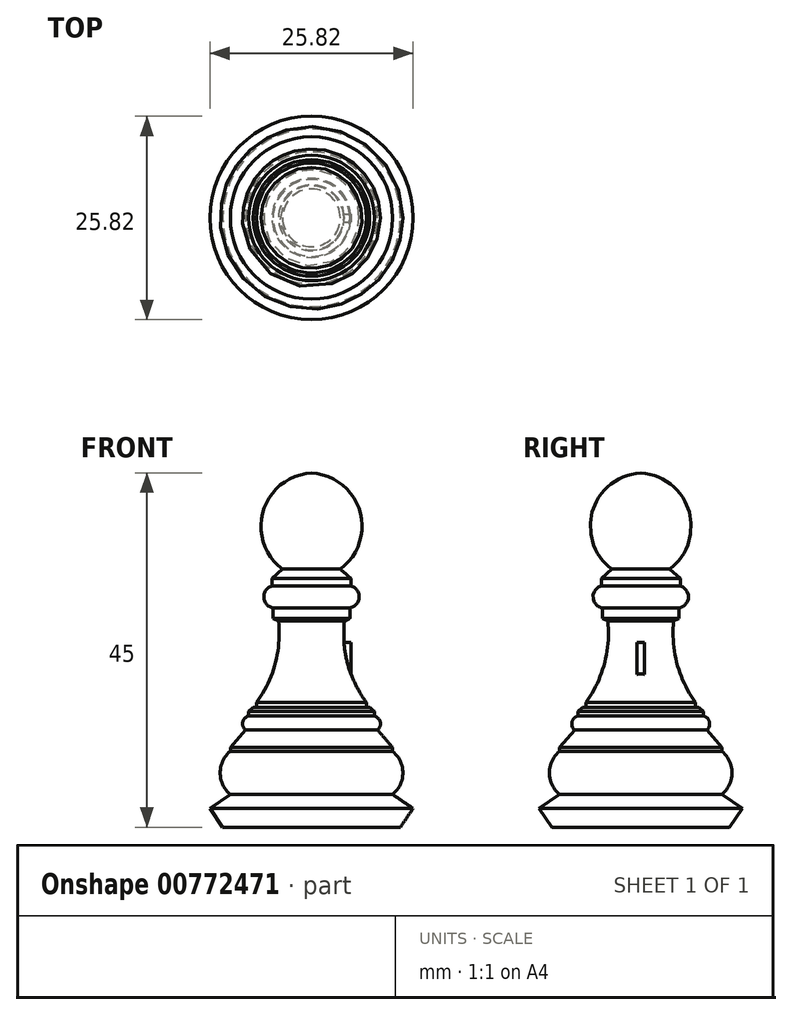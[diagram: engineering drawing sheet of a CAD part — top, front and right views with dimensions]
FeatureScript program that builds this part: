
annotation { "Feature Type Name" : "Feature", "Feature Type Description" : "" }
export const myFeature = defineFeature(function(context is Context, id is Id, definition is map)
    precondition{}
    {
        {
            var Q0;
            Q0=qCreatedBy(makeId("Front.planeOp"),FACE);
            var sketch = newSketch(context, id + "F0", { "sketchPlane" : qUnion([Q0])});
            skLineSegment(sketch, "E0", {"start": v(0, 0) * mm, "end": v(11.29, 0) * mm});
            skLineSegment(sketch, "E1", {"start": v(11.29, 0) * mm, "end": v(12.91, 2.4) * mm});
            skLineSegment(sketch, "E2", {"start": v(12.91, 2.4) * mm, "end": v(10.31, 4.16) * mm});
            skArc(sketch, "E3", {"start": v(10.31, 4.16) * mm, "mid": v(11.6, 6.9) * mm, "end": v(10.31, 9.66) * mm});
            skLineSegment(sketch, "E4", {"start": v(10.31, 9.66) * mm, "end": v(10.31, 10.13) * mm});
            skLineSegment(sketch, "E5", {"start": v(10.31, 10.13) * mm, "end": v(8.38, 12.37) * mm});
            skArc(sketch, "E6", {"start": v(8.38, 12.37) * mm, "mid": v(8.73, 13.38) * mm, "end": v(7.97, 14.14) * mm});
            skLineSegment(sketch, "E7", {"start": v(7.97, 14.14) * mm, "end": v(7.97, 14.74) * mm});
            skLineSegment(sketch, "E8", {"start": v(7.97, 14.74) * mm, "end": v(7.4, 15.25) * mm});
            skLineSegment(sketch, "E9", {"start": v(7.4, 15.25) * mm, "end": v(6.98, 15.25) * mm});
            skLineSegment(sketch, "E10", {"start": v(6.98, 15.83) * mm, "end": v(6.98, 15.25) * mm});
            skArc(sketch, "E11", {"start": v(4.18, 26.19) * mm, "mid": v(4.62, 20.75) * mm, "end": v(6.98, 15.83) * mm});
            skLineSegment(sketch, "E12", {"start": v(4.18, 26.19) * mm, "end": v(4.89, 26.5) * mm});
            skLineSegment(sketch, "E13", {"start": v(4.89, 26.5) * mm, "end": v(4.89, 27.86) * mm});
            skLineSegment(sketch, "E14", {"start": v(5.01, 30.66) * mm, "end": v(5.01, 31.6) * mm});
            skLineSegment(sketch, "E15", {"start": v(5.01, 31.6) * mm, "end": v(3.67, 32.8) * mm});
            skArc(sketch, "E16", {"start": v(3.67, 32.8) * mm, "mid": v(6.13, 40.19) * mm, "end": v(0, 45) * mm});
            skLineSegment(sketch, "E17", {"start": v(0, 45) * mm, "end": v(0, 0) * mm});
            skArc(sketch, "E18", {"start": v(4.89, 27.86) * mm, "mid": v(6.05, 29.2) * mm, "end": v(5.01, 30.66) * mm});
            skSolve(sketch);
        }
        {
            var Q0;
            Q0 = qSketchRegion(id + "F0", true);
            var Q1;
            Q1=sQuery(id+"F0.wireOp",EDGE,"E17");
            revolve(context, id + "F1", {"surfaceOperationType" : NewSurfaceOperationType.NEW, "entities" : qUnion([Q0]), "axis" : qUnion([Q1]), "revolveType" : RevolveType.FULL});
        }
        {
            var Q0;
            Q0=qCreatedBy(makeId("Front.planeOp"),FACE);
            var sketch = newSketch(context, id + "F2", { "sketchPlane" : qUnion([Q0])});
            skLineSegment(sketch, "E19.bottom", {"start": v(3.69, 19.27) * mm, "end": v(5.02, 19.27) * mm});
            skLineSegment(sketch, "E19.top", {"start": v(3.69, 23.5) * mm, "end": v(5.02, 23.5) * mm});
            skLineSegment(sketch, "E19.left", {"start": v(3.69, 19.27) * mm, "end": v(3.69, 23.5) * mm});
            skLineSegment(sketch, "E19.right", {"start": v(5.02, 19.27) * mm, "end": v(5.02, 23.5) * mm});
            skSolve(sketch);
        }
        {
            var Q0;
            Q0 = qSketchRegion(id + "F2", true);
            extrude(context, id + "F3", {"entities" : qUnion([Q0]), "operationType" : NewBodyOperationType.ADD, "endBound" : BoundingType.SYMMETRIC, "depth" : 1 * mm, "offsetDistance" : 25 * mm});
        }
    });
